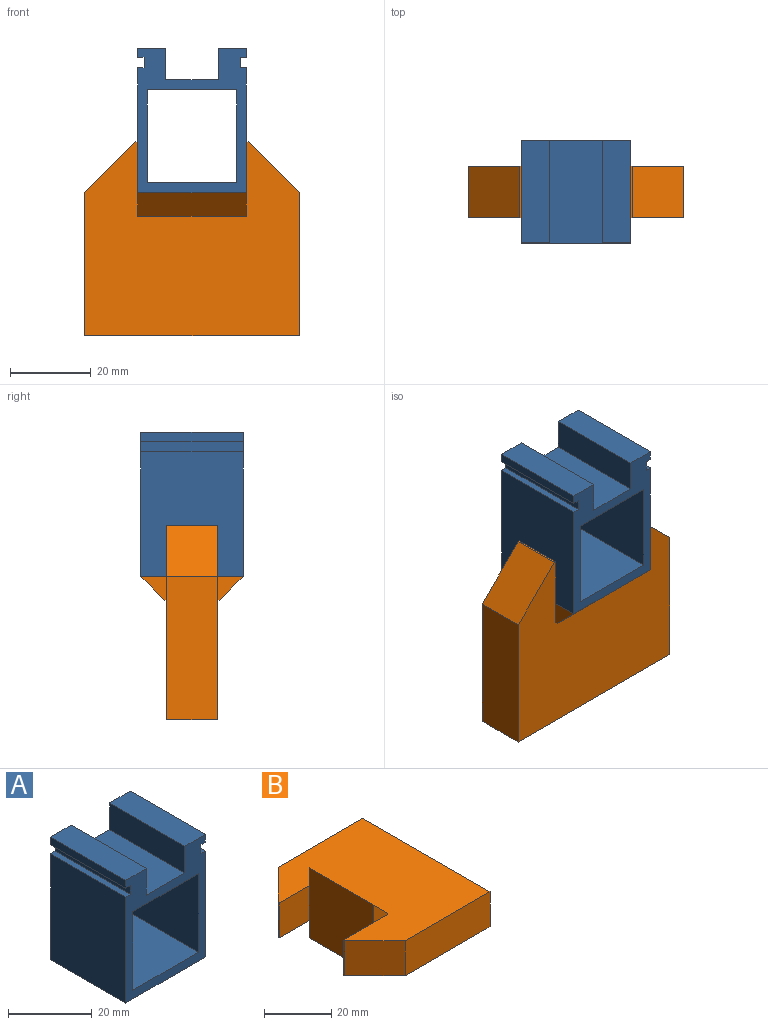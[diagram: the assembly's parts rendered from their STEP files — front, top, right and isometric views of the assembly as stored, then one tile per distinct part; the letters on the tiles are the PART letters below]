
ASSEMBLY  parts=2 mates=1
PART A: 22 faces, bbox 26.9x25.4x35.9 mm
  f0: plane 25.4x2.26mm, normal (1,0,0), area 57.5mm2, adj f2,f3,f14,f20
  f1: plane 25.4x2.26mm, normal (-1,0,0), area 57.5mm2, adj f2,f3,f17,f21
  f2: plane 35.87x26.95mm, normal (0,1,0), area 345.8mm2, adj f0,f1,f4,f5,f6,f7,f8,f9
  f3: plane 35.87x26.95mm, normal (0,-1,0), area 345.8mm2, adj f0,f1,f4,f5,f6,f7,f8,f9
  f4: plane 25.4x13mm, normal (0,0,1), area 330.2mm2, adj f2,f3,f12,f13
  f5: plane 26.95x25.4mm, normal (0,0,-1), area 684.5mm2, adj f2,f3,f6,f11
  f6: plane 30.99x25.4mm, normal (1,0,0), area 787.2mm2, adj f2,f3,f5,f16
  f7: plane 25.4x22.96mm, normal (-1,0,0), area 583.2mm2, adj f2,f3,f8,f10
  f8: plane 25.4x22.28mm, normal (0,0,1), area 565.8mm2, adj f2,f3,f7,f9
  f9: plane 25.4x22.96mm, normal (1,0,0), area 583.2mm2, adj f2,f3,f8,f10
  f10: plane 25.4x22.28mm, normal (0,0,-1), area 565.8mm2, adj f2,f3,f7,f9
  f11: plane 30.99x25.4mm, normal (-1,0,0), area 787.2mm2, adj f2,f3,f5,f18
  f12: plane 25.4x7.8mm, normal (1,0,0), area 198.2mm2, adj f2,f3,f4,f21
  f13: plane 25.4x7.8mm, normal (-1,0,0), area 198.2mm2, adj f2,f3,f4,f20
  f14: plane 25.4x1.5mm, normal (0,0,-1), area 38.2mm2, adj f0,f2,f3,f15
  f15: plane 25.4x2.62mm, normal (1,0,0), area 66.5mm2, adj f2,f3,f14,f16
  f16: plane 25.4x1.5mm, normal (0,0,1), area 38.2mm2, adj f2,f3,f6,f15
  f17: plane 25.4x1.55mm, normal (0,0,-1), area 39.4mm2, adj f1,f2,f3,f19
  f18: plane 25.4x1.55mm, normal (0,0,1), area 39.4mm2, adj f2,f3,f11,f19
  f19: plane 25.4x2.62mm, normal (-1,0,0), area 66.5mm2, adj f2,f3,f17,f18
  f20: plane 25.4x6.98mm, normal (0,0,1), area 177.2mm2, adj f0,f2,f3,f13
  f21: plane 25.4x6.98mm, normal (0,0,1), area 177.2mm2, adj f1,f2,f3,f12
PART B: 31 faces, bbox 48.3x53.3x25.4 mm
  f0: plane 26.95x25.4mm, normal (-1,0,0), area 684.5mm2, adj f17,f20,f23,f25,f26,f27,f29,f30
  f1: plane 53.34x34.29mm, normal (0,0,1), area 1352.5mm2, adj f2,f3,f4,f8,f9,f10,f11,f12
  f2: plane 3.81x3.05mm, normal (0,-1,0), area 11.6mm2, adj f1,f8,f11,f14
  f3: plane 3.81x3.05mm, normal (0,1,0), area 11.6mm2, adj f1,f9,f10,f14
  f4: plane 53.34x4.83mm, normal (1,0,0), area 257.4mm2, adj f1,f5,f6,f7
  f5: plane 35.56x12.7mm, normal (0,1,0), area 451.6mm2, adj f4,f7,f12,f15,f16,f19
  f6: plane 35.56x12.7mm, normal (0,-1,0), area 451.6mm2, adj f4,f7,f13,f15,f16,f22
  f7: plane 53.34x48.26mm, normal (0,0,-1), area 1911.8mm2, adj f4,f5,f6,f17,f18,f19,f20,f21
  f8: plane 24.13x11.43mm, normal (0.9,-0.43,0), area 81.4mm2, adj f1,f2,f9,f14
  f9: plane 24.13x11.43mm, normal (0.9,0.43,0), area 81.4mm2, adj f1,f3,f8,f14
  f10: plane 13.52x3.05mm, normal (-0.11,0.99,0), area 41.5mm2, adj f1,f3,f13,f14
  f11: plane 13.52x3.05mm, normal (-0.11,-0.99,0), area 41.5mm2, adj f1,f2,f12,f14
  f12: cylinder r=5.08mm len=5.53mm, axis (0,0,-1), area 22.8mm2, adj f1,f5,f11,f14
  f13: cylinder r=5.08mm len=5.53mm, axis (0,0,-1), area 22.8mm2, adj f1,f6,f10,f14
  f14: plane 53.34x34.29mm, normal (0,0,-1), area 1352.5mm2, adj f2,f3,f8,f9,f10,f11,f12,f13
  f15: plane 53.34x4.83mm, normal (1,0,0), area 257.4mm2, adj f5,f6,f14,f16
  f16: plane 53.34x48.26mm, normal (0,0,1), area 1911.8mm2, adj f5,f6,f15,f17,f18,f19,f20,f21
  f17: plane 12.7x12.7mm, normal (0,-1,0), area 161.3mm2, adj f0,f7,f16,f18
  f18: plane 12.7x0.5mm, normal (-1,0,0), area 6.3mm2, adj f7,f16,f17,f19
  f19: plane 12.7x12.7mm, normal (-0.71,0.71,0), area 228.1mm2, adj f5,f7,f16,f18
  f20: plane 12.7x12.7mm, normal (0,1,0), area 161.3mm2, adj f0,f7,f16,f21
  f21: plane 12.7x0.5mm, normal (-1,0,0), area 6.3mm2, adj f7,f16,f20,f22
  f22: plane 12.7x12.7mm, normal (-0.71,-0.71,0), area 228.1mm2, adj f6,f7,f16,f21
  f23: plane 6.35x5.89mm, normal (0,1,0), area 20.1mm2, adj f0,f7,f24,f26
  f24: plane 26.95x0.46mm, normal (1,0,0), area 12.3mm2, adj f7,f23,f25,f26
  f25: plane 6.35x5.89mm, normal (0,-1,0), area 20.1mm2, adj f0,f7,f24,f26
  f26: plane 26.95x5.89mm, normal (0.71,0,-0.71), area 224.6mm2, adj f0,f23,f24,f25
  f27: plane 6.35x5.89mm, normal (0,-1,0), area 20.1mm2, adj f0,f16,f28,f30
  f28: plane 26.95x0.46mm, normal (1,0,0), area 12.3mm2, adj f16,f27,f29,f30
  f29: plane 6.35x5.89mm, normal (0,1,0), area 20.1mm2, adj f0,f16,f28,f30
  f30: plane 26.95x5.89mm, normal (0.71,0,0.71), area 224.6mm2, adj f0,f27,f28,f29
PLACE A t=(19.46,-12.74,29.97)mm
PLACE B rot(axis=(-0.58,0.58,0.58),120deg) t=(19.46,-31.79,-1.84)mm
MATE planar B.f0 <-> A.f5  axis (0,0,1) through (19.46,-25.44,15.94)mm
